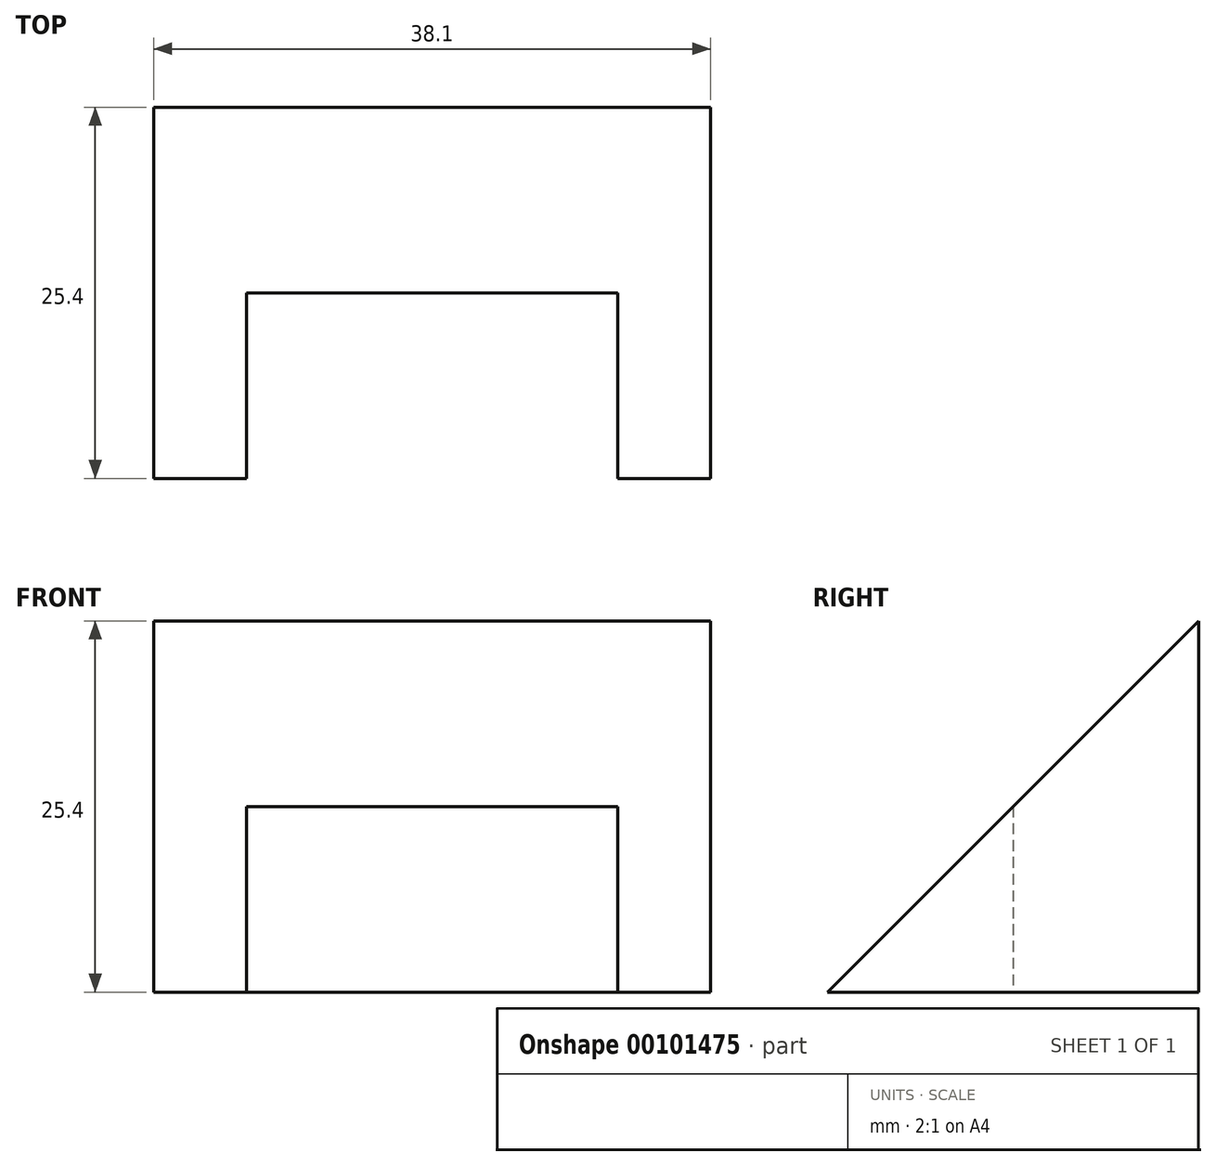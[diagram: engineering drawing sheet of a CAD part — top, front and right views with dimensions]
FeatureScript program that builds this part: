
annotation { "Feature Type Name" : "Feature", "Feature Type Description" : "" }
export const myFeature = defineFeature(function(context is Context, id is Id, definition is map)
    precondition{}
    {
        {
            var Q0;
            Q0=qCreatedBy(makeId("Right.planeOp"),FACE);
            var sketch = newSketch(context, id + "F0", { "sketchPlane" : qUnion([Q0])});
            skLineSegment(sketch, "E0", {"start": v(0, 0) * mm, "end": v(0, 25.4) * mm});
            skLineSegment(sketch, "E1", {"start": v(0, 25.4) * mm, "end": v(-25.4, 0) * mm});
            skLineSegment(sketch, "E2", {"start": v(-25.4, 0) * mm, "end": v(0, 0) * mm});
            skSolve(sketch);
        }
        {
            var Q0;
            Q0=makeQuery(id+"F0.imprint","IMPRINT",FACE,{"disambiguationData":[TD([[makeQuery(id+"F0.imprint","IMPRINT",EDGE,{"derivedFrom":sQuery(id+"F0.wireOp",EDGE,"E0")}),1.0]])]});
            extrude(context, id + "F1", {"entities" : qUnion([Q0]), "depth" : 38.1 * mm});
        }
        {
            var Q0;
            Q0=qCreatedBy(makeId("Top.planeOp"),FACE);
            var sketch = newSketch(context, id + "F2", { "sketchPlane" : qUnion([Q0])});
            skLineSegment(sketch, "E3", {"start": v(0, 0) * mm, "end": v(0, -25.4) * mm});
            skLineSegment(sketch, "E4", {"start": v(0, -25.4) * mm, "end": v(38.1, -25.4) * mm});
            skLineSegment(sketch, "E5", {"start": v(38.1, 0) * mm, "end": v(0, 0) * mm});
            skLineSegment(sketch, "E6", {"start": v(38.1, -25.4) * mm, "end": v(38.1, 0) * mm});
            skLineSegment(sketch, "E7", {"start": v(6.35, -25.4) * mm, "end": v(6.35, -12.7) * mm});
            skLineSegment(sketch, "E8", {"start": v(6.35, -12.7) * mm, "end": v(31.75, -12.7) * mm});
            skLineSegment(sketch, "E9", {"start": v(31.75, -12.7) * mm, "end": v(31.75, -25.4) * mm});
            skLineSegment(sketch, "E10", {"start": v(6.35, -25.4) * mm, "end": v(31.75, -25.4) * mm});
            skSolve(sketch);
        }
        {
            var Q0;
            Q0=makeQuery(id+"F2.imprint","IMPRINT",FACE,{"disambiguationData":[TD([[makeQuery(id+"F2.imprint","IMPRINT",EDGE,{"derivedFrom":sQuery(id+"F2.wireOp",EDGE,"E7")}),-1.0]])]});
            extrude(context, id + "F3", {"entities" : qUnion([Q0]), "operationType" : NewBodyOperationType.REMOVE, "depth" : 12.7 * mm});
        }
    });
